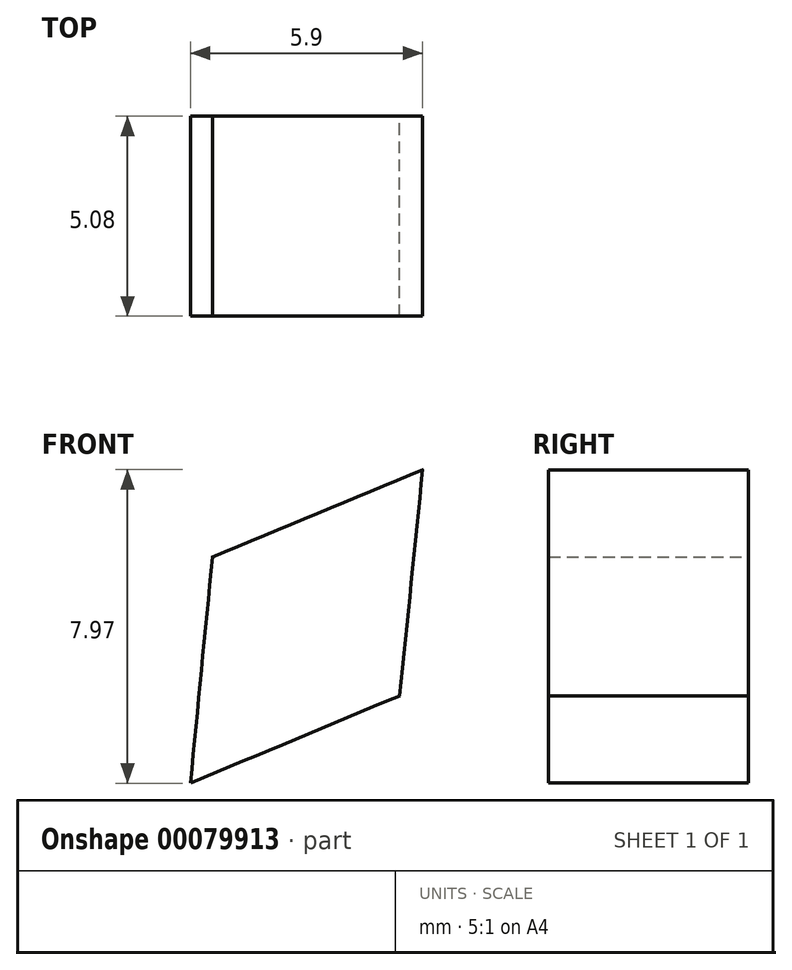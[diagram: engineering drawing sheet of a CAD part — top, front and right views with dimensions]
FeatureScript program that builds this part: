
annotation { "Feature Type Name" : "Feature", "Feature Type Description" : "" }
export const myFeature = defineFeature(function(context is Context, id is Id, definition is map)
    precondition{}
    {
        {
            var Q0;
            Q0=qCreatedBy(makeId("Front.planeOp"),FACE);
            var sketch = newSketch(context, id + "F0", { "sketchPlane" : qUnion([Q0])});
            skFitSpline(sketch, "E0.MirrorCS", {"points": [v(69.85, 59.9) * mm, v(0, 54.85) * mm], "startDerivative": vector(-120.56, -50.12) * mm, "endDerivative": vector(-66.86, 43.53) * mm});
            skFitSpline(sketch, "E1.MirrorCS", {"points": [v(69.85, 59.9) * mm, v(0, -72.15) * mm], "startDerivative": vector(-13.43, -132.62) * mm, "endDerivative": vector(-178.5, -80.58) * mm});
            skFitSpline(sketch, "E2.MirrorCS", {"points": [v(-69.85, 59.9) * mm, v(0, 54.85) * mm], "startDerivative": vector(120.56, -50.12) * mm, "endDerivative": vector(66.86, 43.53) * mm});
            skFitSpline(sketch, "E3.MirrorCS", {"points": [v(-69.85, 59.9) * mm, v(0, -72.15) * mm], "startDerivative": vector(13.43, -132.62) * mm, "endDerivative": vector(178.5, -80.58) * mm});
            skFitSpline(sketch, "E4.0", {"points": [v(-71.8, 55.21) * mm, v(-66.78, 53.13) * mm, v(-57.73, 49.37) * mm, v(-46.54, 45.02) * mm, v(-38.65, 42.5) * mm, v(-32.87, 41.17) * mm, v(-28.71, 40.55) * mm, v(-24.68, 40.33) * mm, v(-20.73, 40.54) * mm, v(-16.85, 41.2) * mm, v(-13.03, 42.29) * mm, v(-9.23, 43.78) * mm, v(-4.12, 46.29) * mm, v(-0.1, 48.72) * mm, v(2.77, 50.59) * mm]});
            skFitSpline(sketch, "E4.1", {"points": [v(-64.8, 60.42) * mm, v(-64.24, 54.89) * mm, v(-63.08, 43.37) * mm, v(-60.62, 25.3) * mm, v(-56.86, 6.99) * mm, v(-51.23, -10.93) * mm, v(-43.18, -27.9) * mm, v(-32.17, -43.37) * mm, v(-17.6, -56.9) * mm, v(-5.03, -64.3) * mm, v(2.1, -67.52) * mm]});
            skFitSpline(sketch, "E4.2", {"points": [v(64.8, 60.42) * mm, v(64.24, 54.89) * mm, v(63.08, 43.37) * mm, v(60.62, 25.3) * mm, v(56.86, 6.99) * mm, v(51.23, -10.93) * mm, v(43.18, -27.9) * mm, v(32.17, -43.37) * mm, v(17.6, -56.9) * mm, v(5.03, -64.3) * mm, v(-2.1, -67.52) * mm]});
            skFitSpline(sketch, "E4.3", {"points": [v(71.8, 55.21) * mm, v(66.78, 53.13) * mm, v(57.73, 49.37) * mm, v(46.54, 45.02) * mm, v(38.65, 42.5) * mm, v(32.87, 41.17) * mm, v(28.71, 40.55) * mm, v(24.68, 40.33) * mm, v(20.73, 40.54) * mm, v(16.85, 41.2) * mm, v(13.03, 42.29) * mm, v(9.23, 43.78) * mm, v(4.12, 46.29) * mm, v(0.1, 48.72) * mm, v(-2.77, 50.59) * mm]});
            skLineSegment(sketch, "E5", {"start": v(-45.86, -32.23) * mm, "end": v(45.86, -32.23) * mm, "construction": true});
            skSolve(sketch);
        }
        {
            var Q0;
            Q0=makeQuery(id+"F0.imprint","IMPRINT",FACE,{"disambiguationData":[TD([[makeQuery(id+"F0.imprint","IMPRINT",EDGE,{"derivedFrom":sQuery(id+"F0.wireOp",EDGE,"E0.MirrorCS")}),1.0]])]});
            extrude(context, id + "F1", {"entities" : qUnion([Q0]), "depth" : 5.08 * mm});
        }
    });
